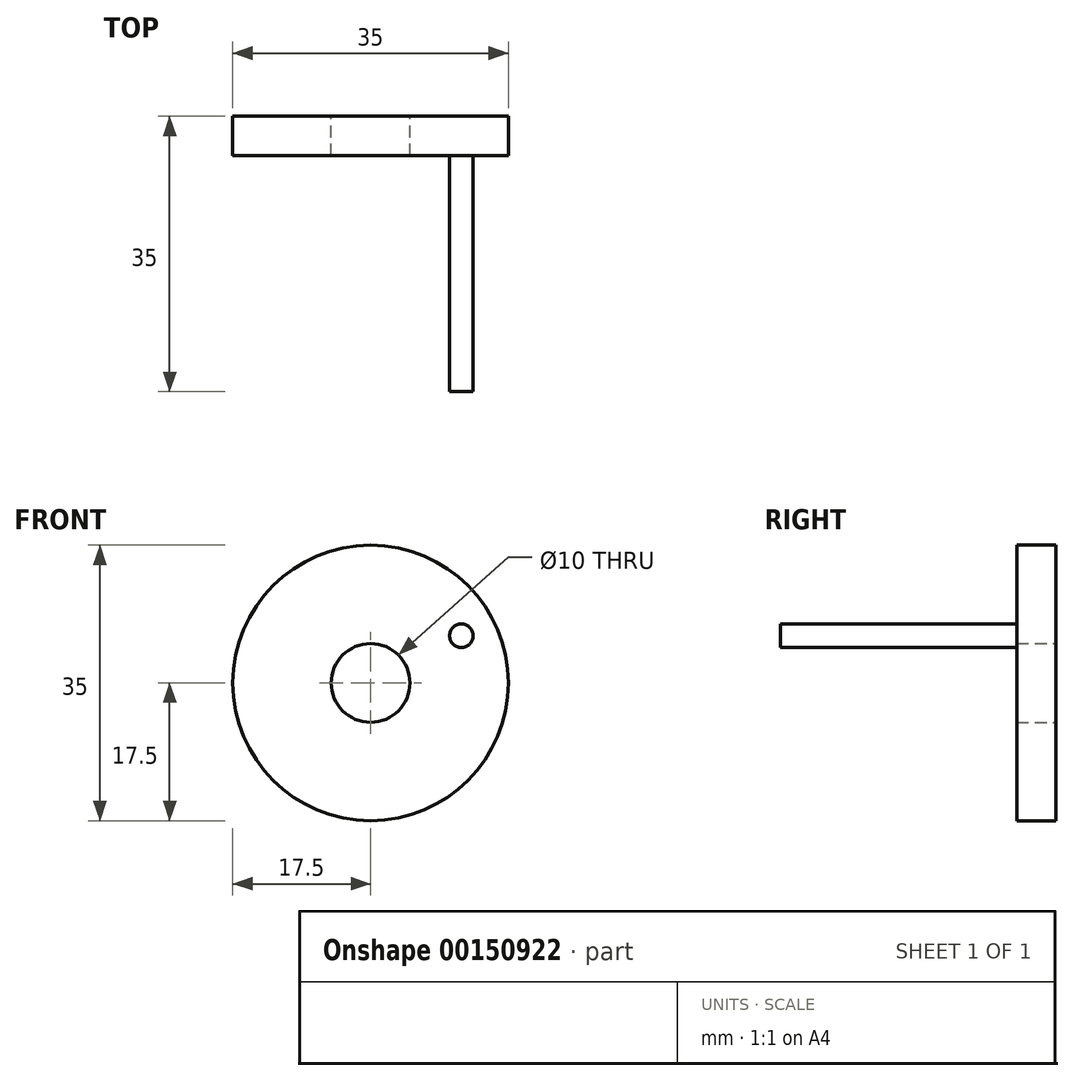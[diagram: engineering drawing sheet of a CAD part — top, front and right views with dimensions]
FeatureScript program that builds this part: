
annotation { "Feature Type Name" : "Feature", "Feature Type Description" : "" }
export const myFeature = defineFeature(function(context is Context, id is Id, definition is map)
    precondition{}
    {
        {
            var Q0;
            Q0=qCreatedBy(makeId("Front.planeOp"),FACE);
            var sketch = newSketch(context, id + "F0", { "sketchPlane" : qUnion([Q0])});
            skCircle(sketch, "E0", {"center": v(0, 0) * mm, "radius": 17.5 * mm});
            skSolve(sketch);
        }
        {
            var Q0;
            Q0=makeQuery(id+"F0.imprint","IMPRINT",FACE,{"disambiguationData":[TD([[makeQuery(id+"F0.imprint","IMPRINT",EDGE,{"derivedFrom":sQuery(id+"F0.wireOp",EDGE,"E0")}),1.0]])]});
            extrude(context, id + "F1", {"entities" : qUnion([Q0]), "depth" : 5 * mm});
        }
        {
            var Q0;
            Q0=makeQuery(id+"F1.opExtrude","CAP_FACE",FACE,{"disambiguationData":[OSD([sQuery(id+"F0.wireOp",EDGE,"E0")])],"isStart":false});
            var sketch = newSketch(context, id + "F2", { "sketchPlane" : qUnion([Q0])});
            skCircle(sketch, "E1", {"center": v(11.53, 6) * mm, "radius": 1.5 * mm});
            skSolve(sketch);
        }
        {
            var Q0;
            Q0=makeQuery(id+"F2.imprint","IMPRINT",FACE,{"disambiguationData":[TD([[makeQuery(id+"F2.imprint","IMPRINT",EDGE,{"derivedFrom":sQuery(id+"F2.wireOp",EDGE,"E1")}),1.0]])]});
            var Q1;
            Q1=sQuery(id+"F2.wireOp",EDGE,"E1");
            extrude(context, id + "F3", {"entities" : qUnion([Q0]), "operationType" : NewBodyOperationType.ADD, "surfaceEntities" : qUnion([Q1]), "depth" : 30 * mm});
        }
        {
            var Q0;
            Q0=qCreatedBy(makeId("Front.planeOp"),FACE);
            var sketch = newSketch(context, id + "F4", { "sketchPlane" : qUnion([Q0])});
            skPoint(sketch, "E2", {"position": v(0, 0) * mm});
            skSolve(sketch);
        }
        {
            var Q0;
            Q0=sQuery(id+"F4.wireOp",VERTEX,"E2");
            var Q1;
            Q1=makeQuery(id+"F1.opExtrude","SWEPT_BODY",BODY,{"disambiguationData":[OSD([sQuery(id+"F0.wireOp",EDGE,"E0")])]});
            hole(context, id + "F5", {"style" : HoleStyle.SIMPLE, "endStyle" : HoleEndStyle.THROUGH, "oppositeDirection" : true, "holeDiameter" : 10 * mm, "locations" : qUnion([Q0]), "scope" : qUnion([Q1]), "isTappedThrough" : true});
        }
    });
